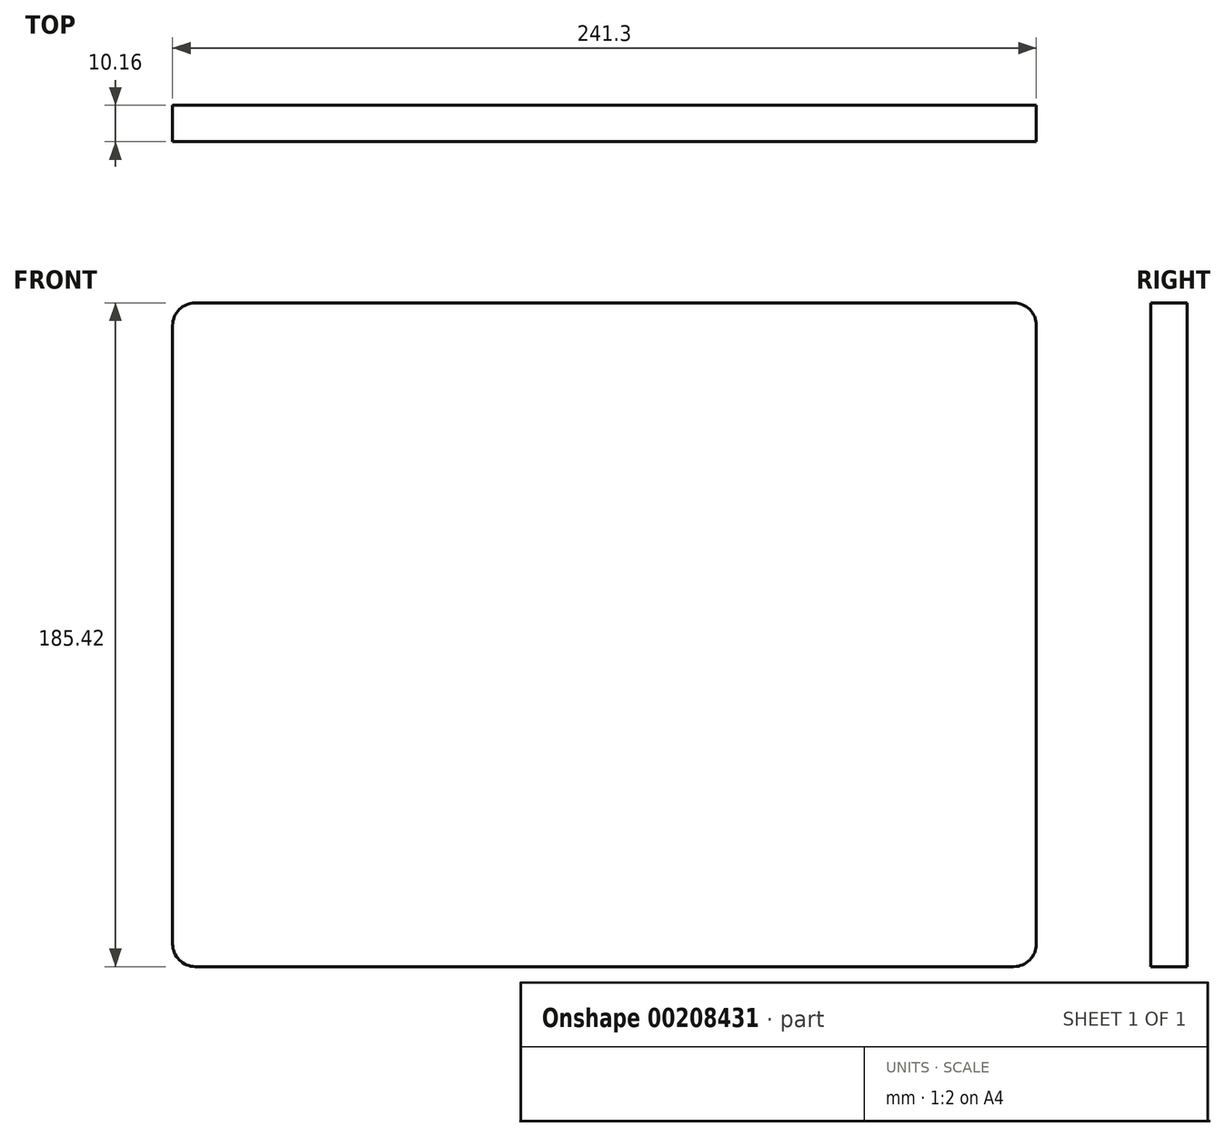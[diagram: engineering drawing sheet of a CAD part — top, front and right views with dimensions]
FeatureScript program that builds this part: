
annotation { "Feature Type Name" : "Feature", "Feature Type Description" : "" }
export const myFeature = defineFeature(function(context is Context, id is Id, definition is map)
    precondition{}
    {
        {
            var Q0;
            Q0=qCreatedBy(makeId("Front.planeOp"),FACE);
            var sketch = newSketch(context, id + "F0", { "sketchPlane" : qUnion([Q0])});
            skLineSegment(sketch, "E0.bottom", {"start": v(114.3, 92.71) * mm, "end": v(-114.3, 92.71) * mm});
            skLineSegment(sketch, "E0.top", {"start": v(114.3, -92.71) * mm, "end": v(-114.3, -92.71) * mm});
            skLineSegment(sketch, "E0.left", {"start": v(120.65, 86.36) * mm, "end": v(120.65, -86.36) * mm});
            skLineSegment(sketch, "E0.right", {"start": v(-120.65, 86.36) * mm, "end": v(-120.65, -86.36) * mm});
            skPoint(sketch, "E0.middle", {"position": v(0, 0) * mm});
            skPoint(sketch, "E1.visualSharp", {"position": v(-120.65, 92.71) * mm});
            skArc(sketch, "E1.filletArc", {"start": v(-114.3, 92.71) * mm, "mid": v(-118.8, 90.85) * mm, "end": v(-120.65, 86.36) * mm});
            skPoint(sketch, "E2.visualSharp", {"position": v(120.65, 92.71) * mm});
            skArc(sketch, "E2.filletArc", {"start": v(120.65, 86.36) * mm, "mid": v(118.8, 90.85) * mm, "end": v(114.3, 92.71) * mm});
            skPoint(sketch, "E3.visualSharp", {"position": v(120.65, -92.71) * mm});
            skArc(sketch, "E3.filletArc", {"start": v(114.3, -92.71) * mm, "mid": v(118.8, -90.85) * mm, "end": v(120.65, -86.36) * mm});
            skPoint(sketch, "E4.visualSharp", {"position": v(-120.65, -92.71) * mm});
            skArc(sketch, "E4.filletArc", {"start": v(-120.65, -86.36) * mm, "mid": v(-118.8, -90.85) * mm, "end": v(-114.3, -92.71) * mm});
            skSolve(sketch);
        }
        {
            var Q0;
            Q0=qSketchRegion(id+"F0",true);
            extrude(context, id + "F1", {"entities" : qUnion([Q0]), "depth" : 10.16 * mm});
        }
    });
